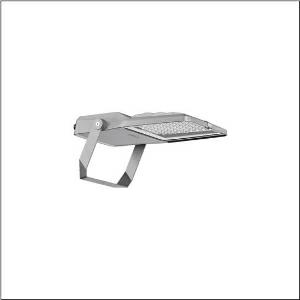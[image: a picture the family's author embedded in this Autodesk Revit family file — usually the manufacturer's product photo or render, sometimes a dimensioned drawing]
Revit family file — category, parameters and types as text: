
# Revit family: floodlight_fl_21_mini___pl61_5xa7776b4c1a_e5f9
name_source: partatom
category: Lighting Fixtures
units: mm (PartAtom-declared; Revit-internal decimal feet)

## family parameters
Cut with Voids When Loaded = No
Host = Face
Light Source = No
Part Type = Normal
Room Calculation Point = No
Round Connector Dimension = Use Diameter
Shared = No

## types (1)
- --- (1 x LED, 6360 lm, 45.7 W, 4000K)
    Apparent Load = 46 VA
    CIE Flux Codes = 33 65 98 100 100
    Color Rendering = 70
    Color Temperature = 4000K
    Default Elevation = 1800 mm
    Description = Floodlight FL 21 mini, floodlight, primary light control with lens, of PMMA, primary optical cover: protective disc, of toughened safety glass, transparent, light distribution: PL61, light emission: direct distribution, installation type: surface-mounted, LED, High Power LED, rated luminous flux: 6.360lm, luminous efficacy: 139lm/W, light colour: 740, colour temperature: 4000K, control gear: D4iSmart Interface (Zhaga), control: overheat protection, constant luminous flux control, time-dependent luminous flux control, flexible luminous flux parameterisation, pre-setting: logarithmic dimming characteristic, with terminal, 6-pole, mains connection: 220..240V, AC, 50/60Hz, start of lifetime: 46W, end of service life: 48W, reduction: 22W, mounting bracket, of diecast aluminium, powder-coated, Siteco® metallic grey (DB 702S), corrosivity category C5 mid according to DIN EN ISO 12944, chlorine-resistant, suitable for swimming pools, sealing non-destructively replaceable, mounting bracket, of steel, galvanised, powder-coated, Siteco® metallic grey (DB 702S), Smart Interface below and above, protection rating (complete): IP66, insulation class (complete): insulation class II (safety insulation), certification: CE, ENEC, VDE, protection symbol: D, impact resistance: IK08, permissible operating ambient temperature: -40..+40°C, permissible operating ambient temperature for outdoor applications: -40..+50°C, standard: DIN EN 12944, LABS conformity tested according to VDMA 24364:2018-05, packaging unit: 1 piece

Light Distribution: PL61
    Height = 70 mm
    Lamp = 1 x LED
    Lamp Light Flux = 6360 lm
    Lamp Power = 45.7 W
    Lamp count = 1
    Length = 485 mm
    Luminous efficacy = 139 lm/W
    Manufacturer = Siteco
    ModVariant = No
    Model = 5XA7776B4C1A
    Number of Poles = 1
    OnlyDefault = Yes
    Power Factor = 1
    Product Name = Floodlight FL 21 mini | PL61
    Product group = floodlight | pylon annexe
    ProductGroupID = 6200
    Protection Class = Protection class II
    Protection Degree = IP 66
    RLX_Detail_Level = 1
    RLX_Emergency_Light_Flux = 0 lm
    RLX_Emergency_Type = 0
    RLX_Emergency_Type_DB = No
    RlxData = <blob elided: 96025 chars, md5=69ba7b64>
    Socket = socket
    Standby Power = 0 W
    System Light Flux = 6360 lm
    System Power = 46 W
    Type Comments = factory setting: luminous flux: 100 % | dim-lin: 254 | 463 mA
    Type Image = l_1006845.jpg
    URL = http://relux.com
    VarID = @adj_100646
    Voltage = 0 V
    Weight = 0.00 kg
    Width = 337 mm

## geometry (parser evidence)
native form markers: Blend x4, Sweep x12
no freeform markers — native parametric forms only
